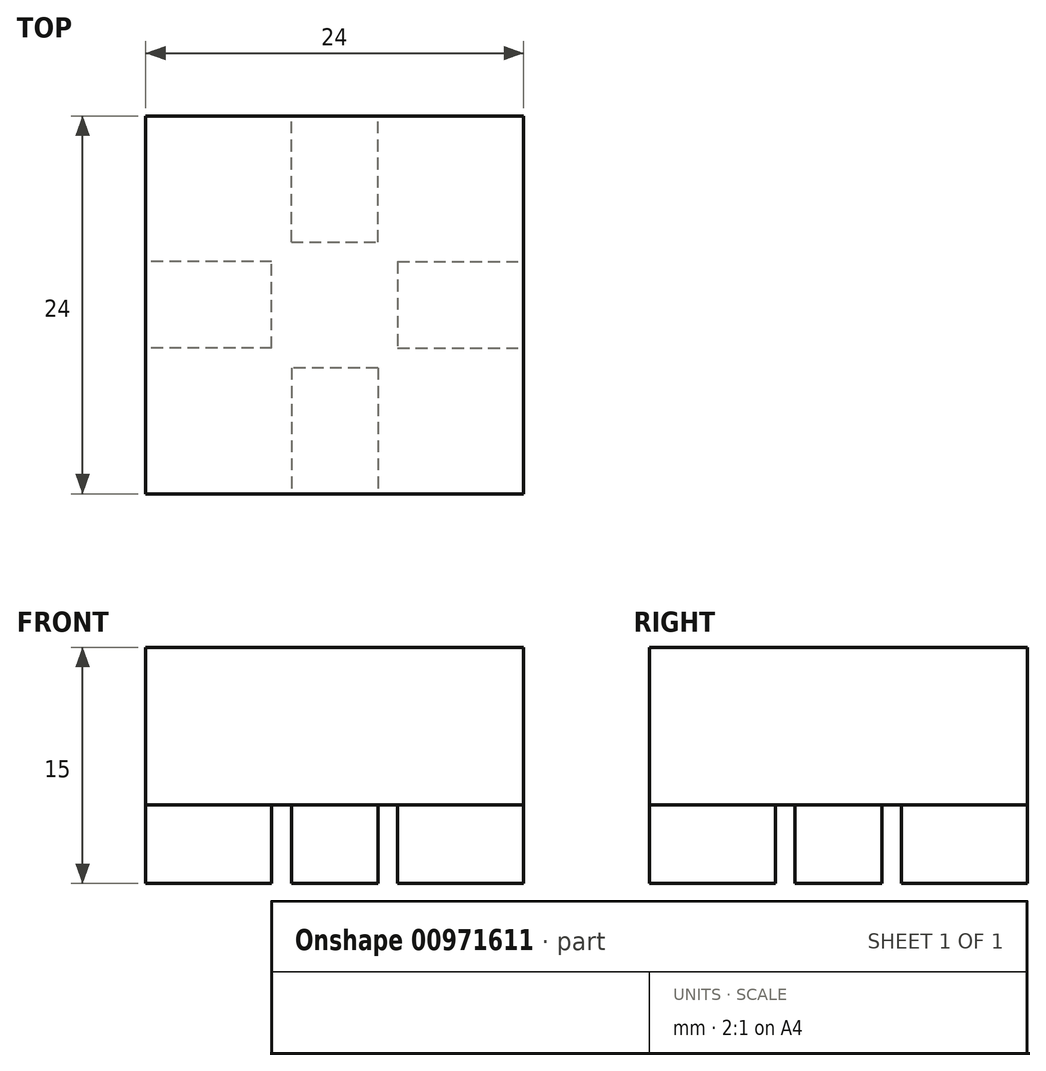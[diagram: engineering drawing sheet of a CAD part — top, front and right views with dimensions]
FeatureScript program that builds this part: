
annotation { "Feature Type Name" : "Feature", "Feature Type Description" : "" }
export const myFeature = defineFeature(function(context is Context, id is Id, definition is map)
    precondition{}
    {
        {
            var Q0;
            Q0=qCreatedBy(makeId("Top.planeOp"),FACE);
            var sketch = newSketch(context, id + "F0", { "sketchPlane" : qUnion([Q0])});
            skLineSegment(sketch, "E0.bottom", {"start": v(-2.75, 4) * mm, "end": v(2.75, 4) * mm});
            skLineSegment(sketch, "E0.top", {"start": v(-2.75, 12) * mm, "end": v(2.75, 12) * mm});
            skLineSegment(sketch, "E0.left", {"start": v(-2.75, 4) * mm, "end": v(-2.75, 12) * mm});
            skLineSegment(sketch, "E0.right", {"start": v(2.75, 4) * mm, "end": v(2.75, 12) * mm});
            skPoint(sketch, "E1", {"position": v(0, 4) * mm});
            skCircle(sketch, "E2", {"center": v(0, 0) * mm, "radius": 1 * mm});
            skSolve(sketch);
        }
        {
            var Q0;
            Q0=makeQuery(id+"F0.imprint","IMPRINT",FACE,{"disambiguationData":[TD([[makeQuery(id+"F0.imprint","IMPRINT",EDGE,{"derivedFrom":sQuery(id+"F0.wireOp",EDGE,"E0.bottom")}),1.0]])]});
            var Q1;
            Q1=makeQuery(id+"F0.imprint","IMPRINT",FACE,{"disambiguationData":[TD([[makeQuery(id+"F0.imprint","IMPRINT",EDGE,{"derivedFrom":sQuery(id+"F0.wireOp",EDGE,"E2")}),1.0]])]});
            extrude(context, id + "F1", {"entities" : qUnion([Q0, Q1]), "depth" : 5 * mm, "offsetDistance" : 25 * mm});
        }
        {
            var Q0;
            Q0=makeQuery(id+"F1.opExtrude","SWEPT_BODY",BODY,{"disambiguationData":[OSD([sQuery(id+"F0.wireOp",EDGE,"E0.bottom"),sQuery(id+"F0.wireOp",EDGE,"E0.top"),sQuery(id+"F0.wireOp",EDGE,"E0.left"),sQuery(id+"F0.wireOp",EDGE,"E0.right")])]});
            var Q1;
            Q1=makeQuery(id+"F1.opExtrude","SWEPT_FACE",FACE,{"disambiguationData":[OSD([sQuery(id+"F0.wireOp",EDGE,"E2")])]});
            circularPattern(context, id + "F2", {"entities" : qUnion([Q0]), "axis" : qUnion([Q1]), "angle" : 360 * degree, "instanceCount" : 4, "equalSpace" : true});
        }
        {
            var Q0;
            Q0=makeQuery(id+"F1.opExtrude","SWEPT_BODY",BODY,{"disambiguationData":[OSD([sQuery(id+"F0.wireOp",EDGE,"E2")])]});
            deleteBodies(context, id + "F3", {"entities" : qUnion([Q0])});
        }
        {
            var Q0;
            Q0=makeQuery(id+"F2.opPattern","COPY",FACE,{"derivedFrom":makeQuery(id+"F1.opExtrude","CAP_FACE",FACE,{"disambiguationData":[OSD([sQuery(id+"F0.wireOp",EDGE,"E0.bottom"),sQuery(id+"F0.wireOp",EDGE,"E0.top"),sQuery(id+"F0.wireOp",EDGE,"E0.left"),sQuery(id+"F0.wireOp",EDGE,"E0.right")])],"isStart":false}),"instanceName":"3"});
            var sketch = newSketch(context, id + "F4", { "sketchPlane" : qUnion([Q0])});
            skLineSegment(sketch, "E3.0.0", {"start": v(2.75, 12) * mm, "end": v(-2.75, 12) * mm});
            skLineSegment(sketch, "E3.0.1", {"start": v(-2.75, 12) * mm, "end": v(-2.75, 4) * mm});
            skLineSegment(sketch, "E3.0.2", {"start": v(-2.75, 4) * mm, "end": v(2.75, 4) * mm});
            skLineSegment(sketch, "E3.0.3", {"start": v(2.75, 4) * mm, "end": v(2.75, 12) * mm});
            skLineSegment(sketch, "E4.0.0", {"start": v(12, -2.75) * mm, "end": v(12, 2.75) * mm});
            skLineSegment(sketch, "E4.0.1", {"start": v(12, 2.75) * mm, "end": v(4, 2.75) * mm});
            skLineSegment(sketch, "E4.0.2", {"start": v(4, 2.75) * mm, "end": v(4, -2.75) * mm});
            skLineSegment(sketch, "E4.0.3", {"start": v(4, -2.75) * mm, "end": v(12, -2.75) * mm});
            skLineSegment(sketch, "E5.0.0", {"start": v(-2.75, -12) * mm, "end": v(2.75, -12) * mm});
            skLineSegment(sketch, "E5.0.1", {"start": v(2.75, -12) * mm, "end": v(2.75, -4) * mm});
            skLineSegment(sketch, "E5.0.2", {"start": v(2.75, -4) * mm, "end": v(-2.75, -4) * mm});
            skLineSegment(sketch, "E5.0.3", {"start": v(-2.75, -4) * mm, "end": v(-2.75, -12) * mm});
            skLineSegment(sketch, "E6.0.0", {"start": v(-12, 2.75) * mm, "end": v(-12, -2.75) * mm});
            skLineSegment(sketch, "E6.0.1", {"start": v(-12, -2.75) * mm, "end": v(-4, -2.75) * mm});
            skLineSegment(sketch, "E6.0.2", {"start": v(-4, -2.75) * mm, "end": v(-4, 2.75) * mm});
            skLineSegment(sketch, "E6.0.3", {"start": v(-4, 2.75) * mm, "end": v(-12, 2.75) * mm});
            skLineSegment(sketch, "E7.bottom", {"start": v(-12, -12) * mm, "end": v(12, -12) * mm});
            skLineSegment(sketch, "E7.top", {"start": v(-12, 12) * mm, "end": v(12, 12) * mm});
            skLineSegment(sketch, "E7.left", {"start": v(-12, -12) * mm, "end": v(-12, 12) * mm});
            skLineSegment(sketch, "E7.right", {"start": v(12, -12) * mm, "end": v(12, 12) * mm});
            skSolve(sketch);
        }
        {
            var Q0;
            {var subQ4=sQuery(id+"F4.wireOp",EDGE,"E3.0.1");Q0=makeQuery(id+"F4.imprint","IMPRINT",FACE,{"disambiguationData":[TD([[makeQuery(id+"F4.imprint","IMPRINT",EDGE,{"derivedFrom":subQ4}),-1.0]])]});}
            var Q1;
            {var subQ0=sQuery(id+"F4.wireOp",EDGE,"E3.0.1");Q1=makeQuery(id+"F4.imprint","IMPRINT",FACE,{"disambiguationData":[TD([[makeQuery(id+"F4.imprint","IMPRINT",EDGE,{"derivedFrom":subQ0}),1.0]])]});}
            var Q2;
            {var subQ0=sQuery(id+"F4.wireOp",EDGE,"E4.0.1");Q2=makeQuery(id+"F4.imprint","IMPRINT",FACE,{"disambiguationData":[TD([[makeQuery(id+"F4.imprint","IMPRINT",EDGE,{"derivedFrom":subQ0}),1.0]])]});}
            var Q3;
            {var subQ0=sQuery(id+"F4.wireOp",EDGE,"E5.0.1");Q3=makeQuery(id+"F4.imprint","IMPRINT",FACE,{"disambiguationData":[TD([[makeQuery(id+"F4.imprint","IMPRINT",EDGE,{"derivedFrom":subQ0}),1.0]])]});}
            var Q4;
            {var subQ0=sQuery(id+"F4.wireOp",EDGE,"E6.0.1");Q4=makeQuery(id+"F4.imprint","IMPRINT",FACE,{"disambiguationData":[TD([[makeQuery(id+"F4.imprint","IMPRINT",EDGE,{"derivedFrom":subQ0}),-1.0]])]});}
            extrude(context, id + "F5", {"entities" : qUnion([Q0, Q1, Q2, Q3, Q4]), "depth" : 10 * mm, "offsetDistance" : 25 * mm});
        }
    });
